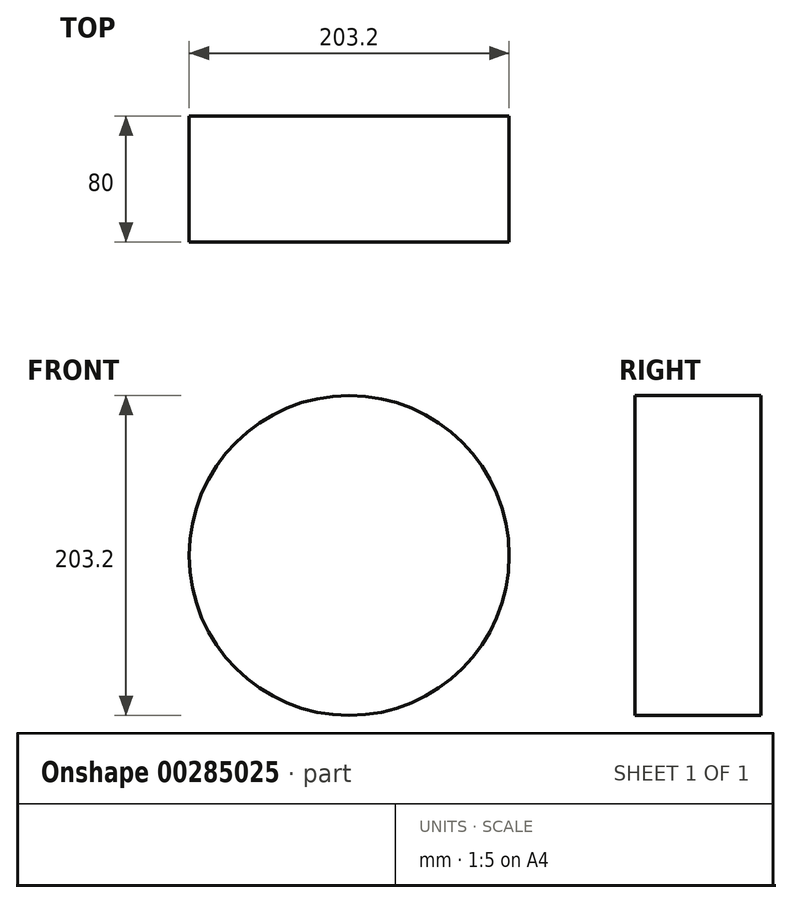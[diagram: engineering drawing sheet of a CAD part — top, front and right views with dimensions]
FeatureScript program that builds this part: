
annotation { "Feature Type Name" : "Feature", "Feature Type Description" : "" }
export const myFeature = defineFeature(function(context is Context, id is Id, definition is map)
    precondition{}
    {
        {
            var Q0;
            Q0=qCreatedBy(makeId("Front.planeOp"),FACE);
            var sketch = newSketch(context, id + "F0", { "sketchPlane" : qUnion([Q0])});
            skCircle(sketch, "E0", {"center": v(0, 0) * mm, "radius": 101.6 * mm});
            skSolve(sketch);
        }
        {
            var Q0;
            Q0=makeQuery(id+"F0.imprint","IMPRINT",FACE,{"disambiguationData":[TD([[makeQuery(id+"F0.imprint","IMPRINT",EDGE,{"derivedFrom":sQuery(id+"F0.wireOp",EDGE,"E0")}),1.0]])]});
            extrude(context, id + "F1", {"entities" : qUnion([Q0]), "depth" : 80 * mm});
        }
        {
            var Q0;
            Q0=makeQuery(id+"F1.opExtrude","CAP_FACE",FACE,{"disambiguationData":[OSD([sQuery(id+"F0.wireOp",EDGE,"E0")])],"isStart":false});
            var sketch = newSketch(context, id + "F2", { "sketchPlane" : qUnion([Q0])});
            skLineSegment(sketch, "E1.bottom", {"start": v(90, 70) * mm, "end": v(-90, 70) * mm});
            skLineSegment(sketch, "E1.top", {"start": v(90, -70) * mm, "end": v(-90, -70) * mm});
            skLineSegment(sketch, "E1.left", {"start": v(90, 70) * mm, "end": v(90, -70) * mm});
            skLineSegment(sketch, "E1.right", {"start": v(-90, 70) * mm, "end": v(-90, -70) * mm});
            skPoint(sketch, "E1.middle", {"position": v(0, 0) * mm});
            skSolve(sketch);
        }
    });
